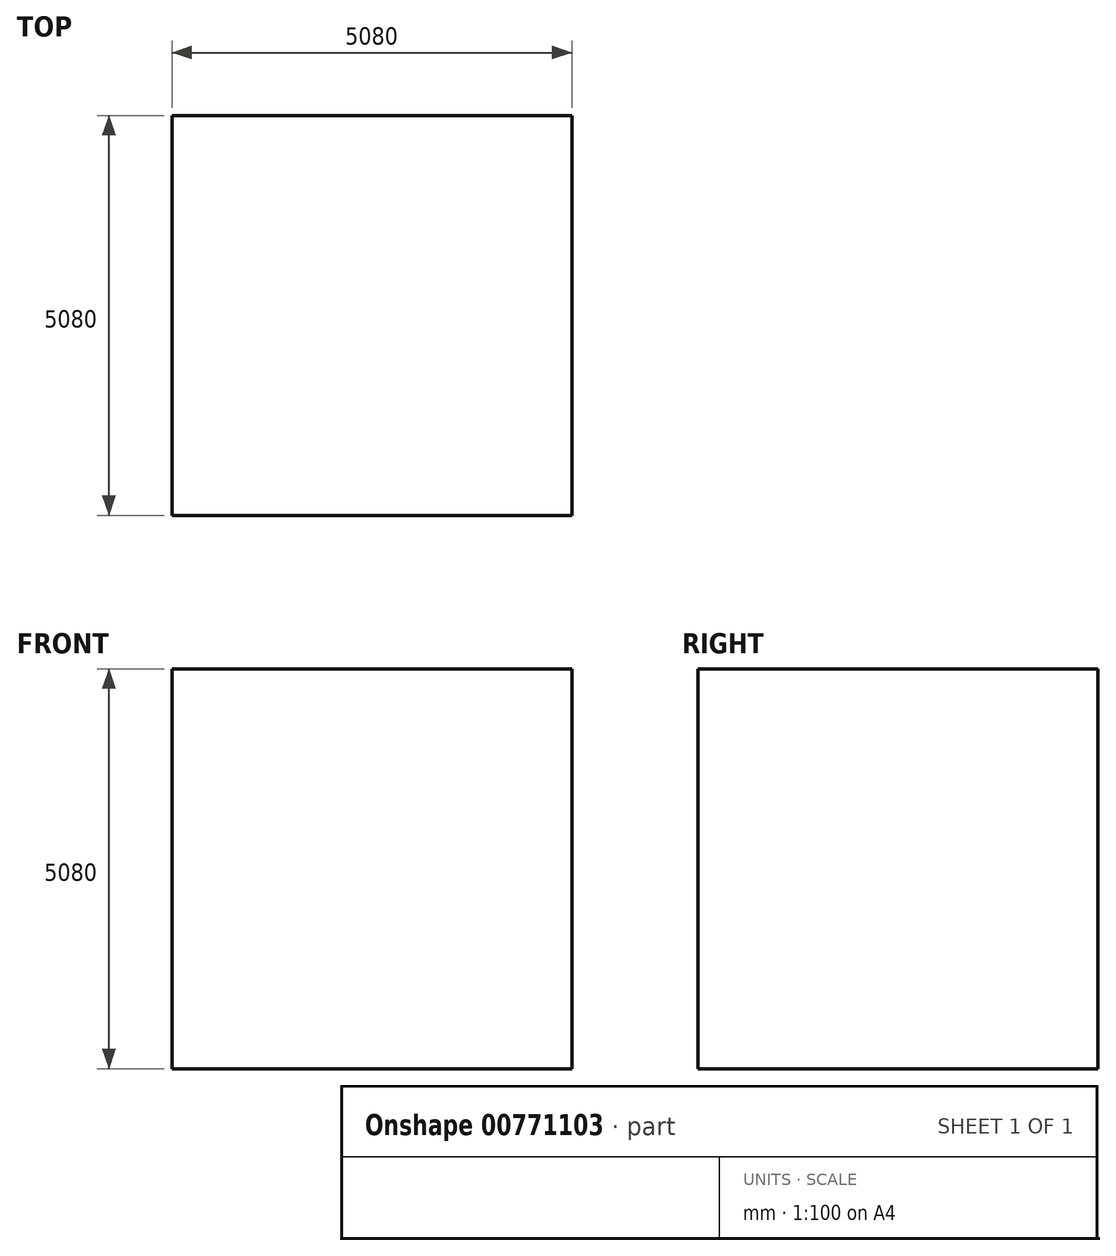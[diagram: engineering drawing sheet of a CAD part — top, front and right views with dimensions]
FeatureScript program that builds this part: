
annotation { "Feature Type Name" : "Feature", "Feature Type Description" : "" }
export const myFeature = defineFeature(function(context is Context, id is Id, definition is map)
    precondition{}
    {
        {
            var Q0;
            Q0=qCreatedBy(makeId("Front.planeOp"),FACE);
            var sketch = newSketch(context, id + "F0", { "sketchPlane" : qUnion([Q0])});
            skLineSegment(sketch, "E0.bottom", {"start": v(0, 0) * mm, "end": v(-5080, 0) * mm});
            skLineSegment(sketch, "E0.top", {"start": v(0, -5080) * mm, "end": v(-5080, -5080) * mm});
            skLineSegment(sketch, "E0.left", {"start": v(0, 0) * mm, "end": v(0, -5080) * mm});
            skLineSegment(sketch, "E0.right", {"start": v(-5080, 0) * mm, "end": v(-5080, -5080) * mm});
            skSolve(sketch);
        }
        {
            var Q0;
            Q0 = qSketchRegion(id + "F0", true);
            extrude(context, id + "F1", {"entities" : qUnion([Q0]), "depth" : 5080 * mm, "offsetDistance" : 25.4 * mm});
        }
    });
